# Revit family: Domotics-DomesticRanges-GEWISS-CHORUS_DATA-SOCKET-OUTLET_COVER_1M
name_source: partatom
category: Apparecchi elettrici
revit_build: Autodesk Revit 2016 (Build: 20161004_0715(x64)
units: mm (PartAtom-declared; Revit-internal decimal feet)

## family parameters
Condiviso = Sì
Host = Superficie
Mantenere orientamento annotazione = Sì
Numero OmniClass = 23.80.50.14
Punto di calcolo locali = Sì
Quota connettore circolare = Usa diametro
Taglio con vuoti quando caricato = Sì
Tipo di parte = Normale
Titolo OmniClass = Plug Connectors

## types (6) — shared parameters
Catalogue = DOMOTICS
Catalogue Range = CHORUS - DOMESTIC RANGE
Category = Adapter
Description. = Adapter
Distanza effettiva_x = 1500 mm  [stored 4.92126 ft]
Electrocod = 0131
IDF = b9c51716-2824-446a-be3e-49b84f176017
IDT = d1aef546-329d-4669-8d08-4aeb95ba3255
Immagine tipo = GW14431.jpg
Larghezza presa = 23 mm  [stored 0.0754593 ft]
No. Chorus modules: = 1
Produttore = GEWISS S.p.A.
Prospetto di default = 1219 mm
SEO = Container
Simbolo = SIMBOLO PRESE TELEFONO : PRESA TEL
Technical sheet = https://www.gewiss.com
Tipo = SYSTEM PRESE RJ45_BASE : RJ45 Titanio
URL = https://www.gewiss.com
Version file RFA = 19.0
zero-valued in all types: Distanza_x

## per-type parameters (varying)
| type | Colour | Compatibility: | Descrizione | EAN code | Modello |
| GW14431 - UNWIRED ENCLOS.RJ45 CONNEC.TITANIUM | Titanium | AMP / Keystone Jack | UNWIRED ENCLOS.RJ45 CONNEC.TITANIUM | 8011564295445 | GW14431 |
| GW10438 - ADAPTER FOR HOUSING DATA CONNECTORS W. | White | SYSTIMAX COMMSCOPE | ADAPTER FOR HOUSING DATA CONNECTORS W. | 8011564719866 | GW10438 |
| GW12431 - UNWIRED ENCLOS.RJ45 CONNEC.BLACK | Black | AMP / Keystone Jack | UNWIRED ENCLOS.RJ45 CONNEC.BLACK | 8011564295438 | GW12431 |
| GW12438 - ADAPTER FOR HOUSING DATA CONNECTORS B. | Black | SYSTIMAX COMMSCOPE | ADAPTER FOR HOUSING DATA CONNECTORS B. | 8011564719873 | GW12438 |
| GW14438 - ADAPTER FOR HOUSING DATA CONNECTORS T. | Titanium | SYSTIMAX COMMSCOPE | ADAPTER FOR HOUSING DATA CONNECTORS T. | 8011564719880 | GW14438 |
| GW10431 - UNWIRED ENCLOS.RJ45 CONNEC. WHITE | White | AMP / Keystone Jack | UNWIRED ENCLOS.RJ45 CONNEC. WHITE | 8011564295421 | GW10431 |

note: [stored X ft] marks values corroborated as IEEE doubles in the binary element streams (Revit-internal decimal feet)

## geometry (parser evidence)
native form markers: Sweep x1
no freeform markers — native parametric forms only
